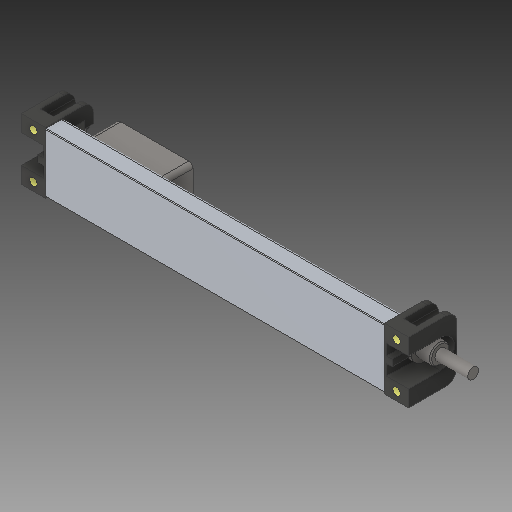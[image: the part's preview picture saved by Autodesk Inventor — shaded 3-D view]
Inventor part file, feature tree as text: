
AUTODESK INVENTOR PART (.ipt)
format: ipt  version: 2019 (Build 230136000, 136)  size: 544,256 bytes
history: native  units: mm
features: other x4, sketch x1
ambient origin geometry x8: Origin, YZ Plane, XZ Plane, XY Plane, X Axis, Y Axis, Z Axis, Center Point
bodies: Solid1 (feature_tree), Solid2 (feature_tree)
feature tree (5):
  other  "SLNV_27_100_2_MIR_MIR.ipt"
  other  "Solid1::SLNV_27_100_2_MIR_MIR.ipt"
  other  "Solid2::SLNV_27_100_2_MIR_MIR.ipt"
  other  "TaggingFeature1"
  sketch  "Sketch1"  dims[d0=10.0mm]
